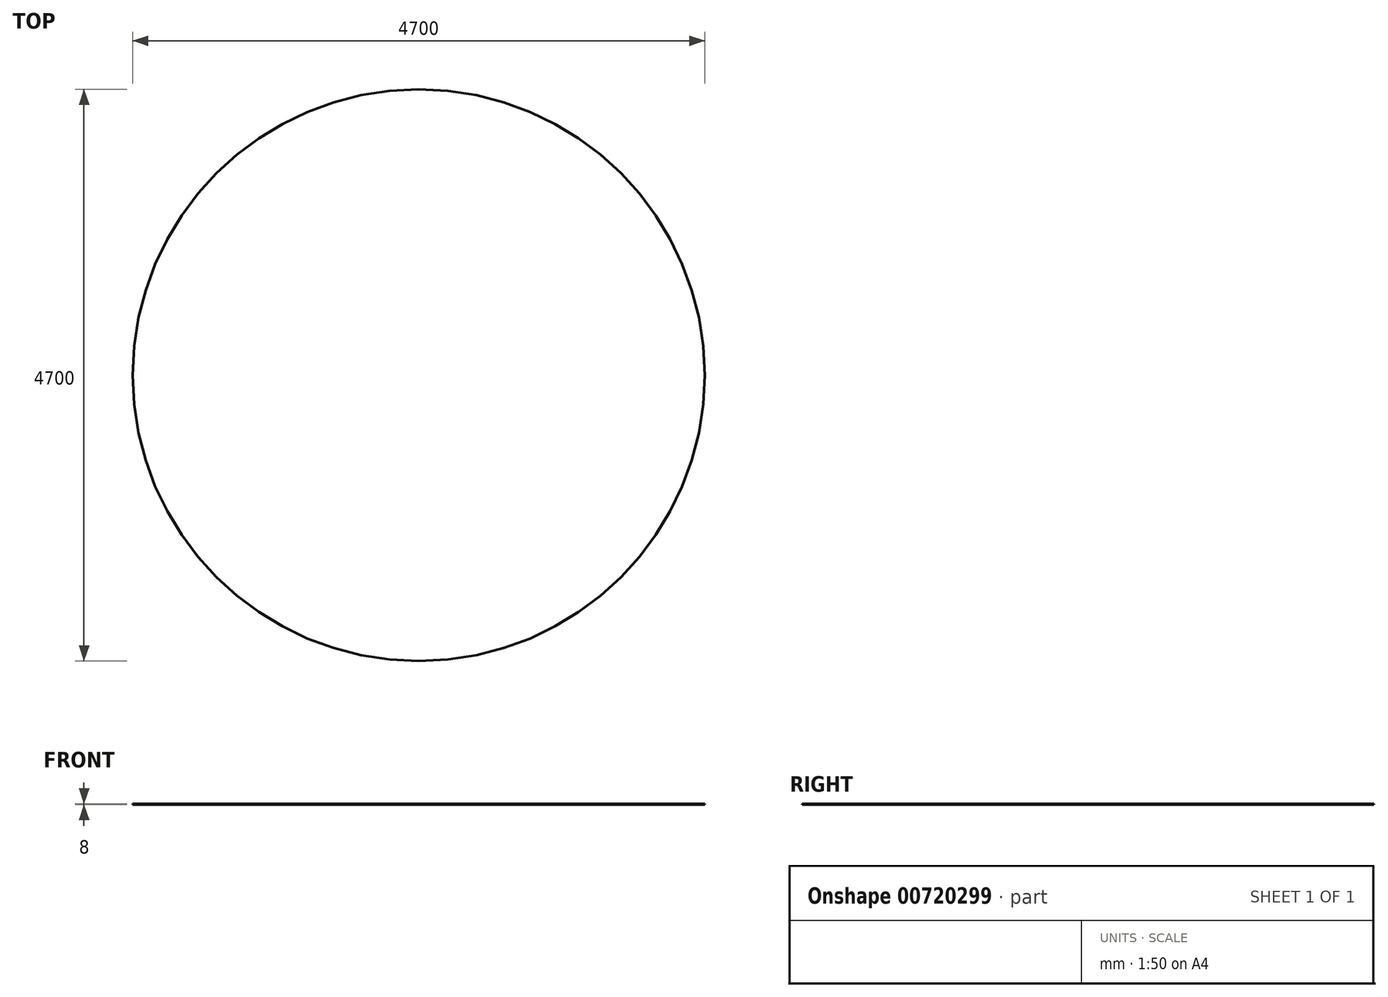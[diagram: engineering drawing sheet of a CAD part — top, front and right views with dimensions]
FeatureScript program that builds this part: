
annotation { "Feature Type Name" : "Feature", "Feature Type Description" : "" }
export const myFeature = defineFeature(function(context is Context, id is Id, definition is map)
    precondition{}
    {
        {
            var Q0;
            Q0=qCreatedBy(makeId("Top.planeOp"),FACE);
            var sketch = newSketch(context, id + "F0", { "sketchPlane" : qUnion([Q0])});
            skCircle(sketch, "E0", {"center": v(0, 0) * mm, "radius": 2350 * mm});
            skSolve(sketch);
        }
        {
            var Q0;
            Q0=makeQuery(id+"F0.imprint","IMPRINT",FACE,{"disambiguationData":[TD([[makeQuery(id+"F0.imprint","IMPRINT",EDGE,{"derivedFrom":sQuery(id+"F0.wireOp",EDGE,"E0")}),1.0]])]});
            extrude(context, id + "F1", {"entities" : qUnion([Q0]), "depth" : 8 * mm, "offsetDistance" : 25 * mm});
        }
    });
